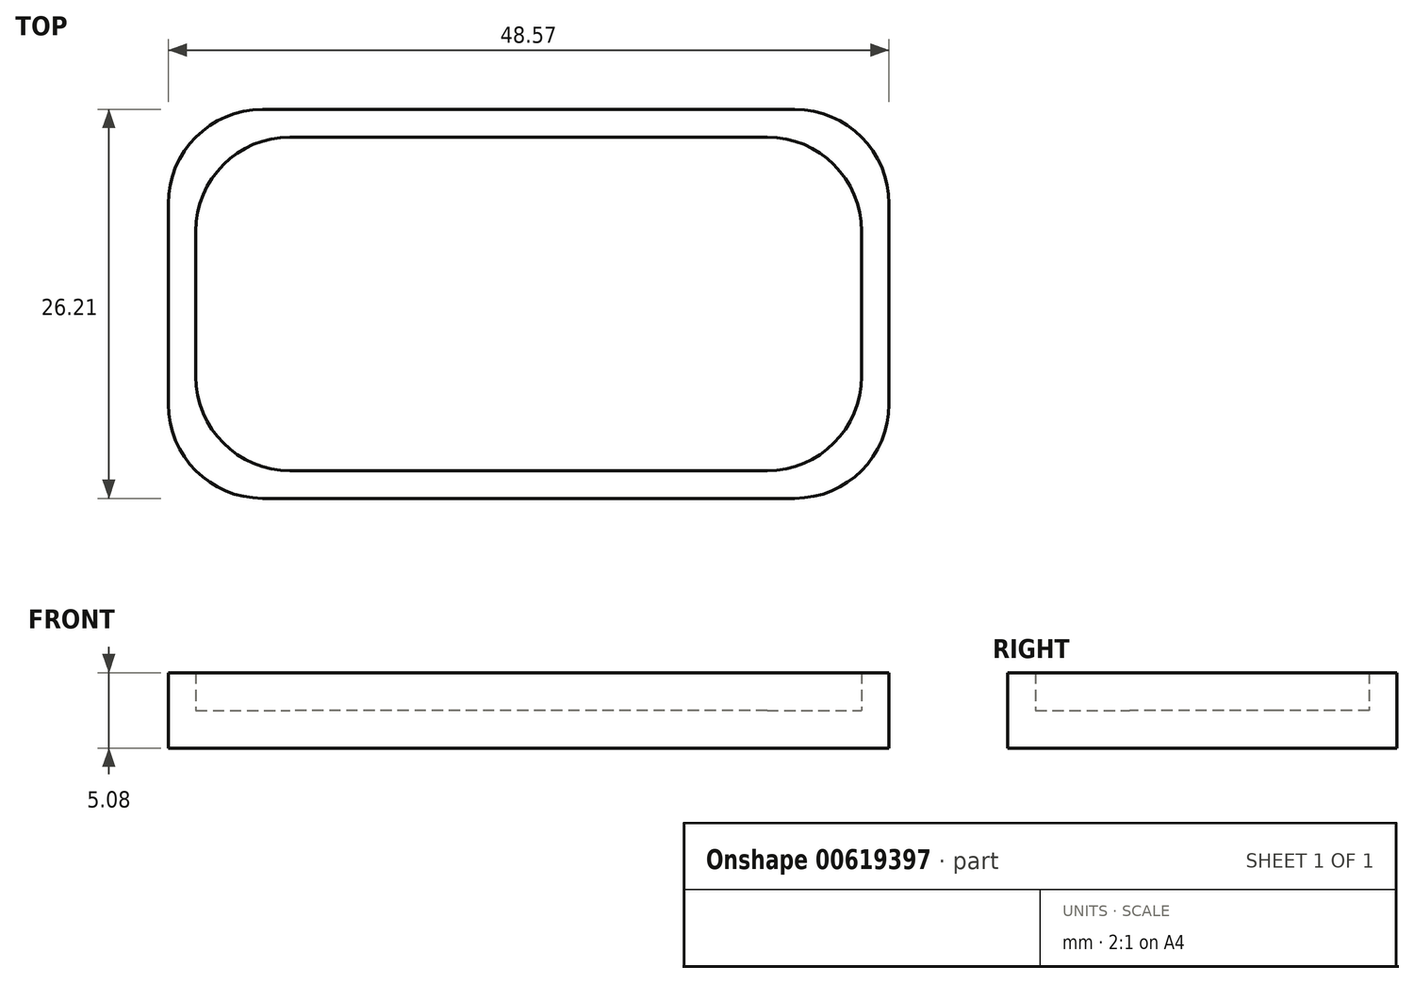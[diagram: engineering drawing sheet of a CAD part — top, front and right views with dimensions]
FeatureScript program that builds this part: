
annotation { "Feature Type Name" : "Feature", "Feature Type Description" : "" }
export const myFeature = defineFeature(function(context is Context, id is Id, definition is map)
    precondition{}
    {
        {
            var Q0;
            Q0=qCreatedBy(makeId("Top.planeOp"),FACE);
            var sketch = newSketch(context, id + "F0", { "sketchPlane" : qUnion([Q0])});
            skLineSegment(sketch, "E0.bottom", {"start": v(-19.66, 15.93) * mm, "end": v(16.2, 15.93) * mm});
            skLineSegment(sketch, "E0.top", {"start": v(-19.66, -10.28) * mm, "end": v(16.2, -10.28) * mm});
            skLineSegment(sketch, "E0.left", {"start": v(-26, 9.58) * mm, "end": v(-26, -3.93) * mm});
            skLineSegment(sketch, "E0.right", {"start": v(22.56, 9.58) * mm, "end": v(22.56, -3.93) * mm});
            skPoint(sketch, "E1.visualSharp", {"position": v(22.56, 15.93) * mm});
            skArc(sketch, "E1.filletArc", {"start": v(22.56, 9.58) * mm, "mid": v(20.7, 14.07) * mm, "end": v(16.2, 15.93) * mm});
            skPoint(sketch, "E2.visualSharp", {"position": v(22.56, -10.28) * mm});
            skArc(sketch, "E2.filletArc", {"start": v(16.2, -10.28) * mm, "mid": v(20.7, -8.42) * mm, "end": v(22.56, -3.93) * mm});
            skPoint(sketch, "E3.visualSharp", {"position": v(-26, 15.93) * mm});
            skArc(sketch, "E3.filletArc", {"start": v(-19.66, 15.93) * mm, "mid": v(-24.15, 14.07) * mm, "end": v(-26, 9.58) * mm});
            skPoint(sketch, "E4.visualSharp", {"position": v(-26, -10.28) * mm});
            skArc(sketch, "E4.filletArc", {"start": v(-26, -3.93) * mm, "mid": v(-24.15, -8.42) * mm, "end": v(-19.66, -10.28) * mm});
            skSolve(sketch);
        }
        {
            var Q0;
            Q0=makeQuery(id+"F0.imprint","IMPRINT",FACE,{"disambiguationData":[TD([[makeQuery(id+"F0.imprint","IMPRINT",EDGE,{"derivedFrom":sQuery(id+"F0.wireOp",EDGE,"E0.bottom")}),-1.0]])]});
            extrude(context, id + "F1", {"entities" : qUnion([Q0]), "depth" : 2.54 * mm, "offsetDistance" : 25.4 * mm});
        }
        {
            var Q0;
            Q0=makeQuery(id+"F1.opExtrude","CAP_FACE",FACE,{"disambiguationData":[OSD([sQuery(id+"F0.wireOp",EDGE,"E0.bottom"),sQuery(id+"F0.wireOp",EDGE,"E0.top"),sQuery(id+"F0.wireOp",EDGE,"E0.left"),sQuery(id+"F0.wireOp",EDGE,"E0.right"),sQuery(id+"F0.wireOp",EDGE,"E1.filletArc"),sQuery(id+"F0.wireOp",EDGE,"E2.filletArc"),sQuery(id+"F0.wireOp",EDGE,"E3.filletArc"),sQuery(id+"F0.wireOp",EDGE,"E4.filletArc")])],"isStart":false});
            var sketch = newSketch(context, id + "F2", { "sketchPlane" : qUnion([Q0])});
            skLineSegment(sketch, "E5", {"start": v(-19.66, 15.93) * mm, "end": v(16.2, 15.93) * mm});
            skLineSegment(sketch, "E6", {"start": v(22.56, 9.58) * mm, "end": v(22.56, -3.93) * mm});
            skLineSegment(sketch, "E7", {"start": v(16.2, -10.28) * mm, "end": v(-19.66, -10.28) * mm});
            skLineSegment(sketch, "E8", {"start": v(-26, -3.93) * mm, "end": v(-26, 9.58) * mm});
            skArc(sketch, "E9", {"start": v(-19.66, 15.93) * mm, "mid": v(-24.15, 14.07) * mm, "end": v(-26, 9.58) * mm});
            skArc(sketch, "E10", {"start": v(22.56, 9.58) * mm, "mid": v(20.7, 14.07) * mm, "end": v(16.2, 15.93) * mm});
            skArc(sketch, "E11", {"start": v(16.2, -10.28) * mm, "mid": v(20.7, -8.42) * mm, "end": v(22.56, -3.93) * mm});
            skArc(sketch, "E12", {"start": v(-26, -3.93) * mm, "mid": v(-24.15, -8.42) * mm, "end": v(-19.66, -10.28) * mm});
            skLineSegment(sketch, "E13.bottom", {"start": v(14.35, 14.07) * mm, "end": v(-17.8, 14.07) * mm});
            skLineSegment(sketch, "E13.top", {"start": v(14.35, -8.42) * mm, "end": v(-17.8, -8.42) * mm});
            skLineSegment(sketch, "E13.left", {"start": v(20.7, 7.72) * mm, "end": v(20.7, -2.07) * mm});
            skLineSegment(sketch, "E13.right", {"start": v(-24.15, 7.72) * mm, "end": v(-24.15, -2.07) * mm});
            skPoint(sketch, "E14.visualSharp", {"position": v(20.7, 14.07) * mm});
            skArc(sketch, "E14.filletArc", {"start": v(20.7, 7.72) * mm, "mid": v(18.84, 12.2) * mm, "end": v(14.35, 14.07) * mm});
            skPoint(sketch, "E15.visualSharp", {"position": v(20.7, -8.42) * mm});
            skArc(sketch, "E15.filletArc", {"start": v(14.35, -8.42) * mm, "mid": v(18.84, -6.56) * mm, "end": v(20.7, -2.07) * mm});
            skPoint(sketch, "E16.visualSharp", {"position": v(-24.15, -8.42) * mm});
            skArc(sketch, "E16.filletArc", {"start": v(-24.15, -2.07) * mm, "mid": v(-22.29, -6.56) * mm, "end": v(-17.8, -8.42) * mm});
            skPoint(sketch, "E17.visualSharp", {"position": v(-24.15, 14.07) * mm});
            skArc(sketch, "E17.filletArc", {"start": v(-17.8, 14.07) * mm, "mid": v(-22.29, 12.2) * mm, "end": v(-24.15, 7.72) * mm});
            skSolve(sketch);
        }
        {
            var Q0;
            Q0=makeQuery(id+"F2.imprint","IMPRINT",FACE,{"disambiguationData":[TD([[makeQuery(id+"F2.imprint","IMPRINT",EDGE,{"derivedFrom":sQuery(id+"F2.wireOp",EDGE,"E5")}),-1.0]])]});
            extrude(context, id + "F3", {"entities" : qUnion([Q0]), "operationType" : NewBodyOperationType.ADD, "depth" : 2.54 * mm, "offsetDistance" : 25.4 * mm});
        }
    });
